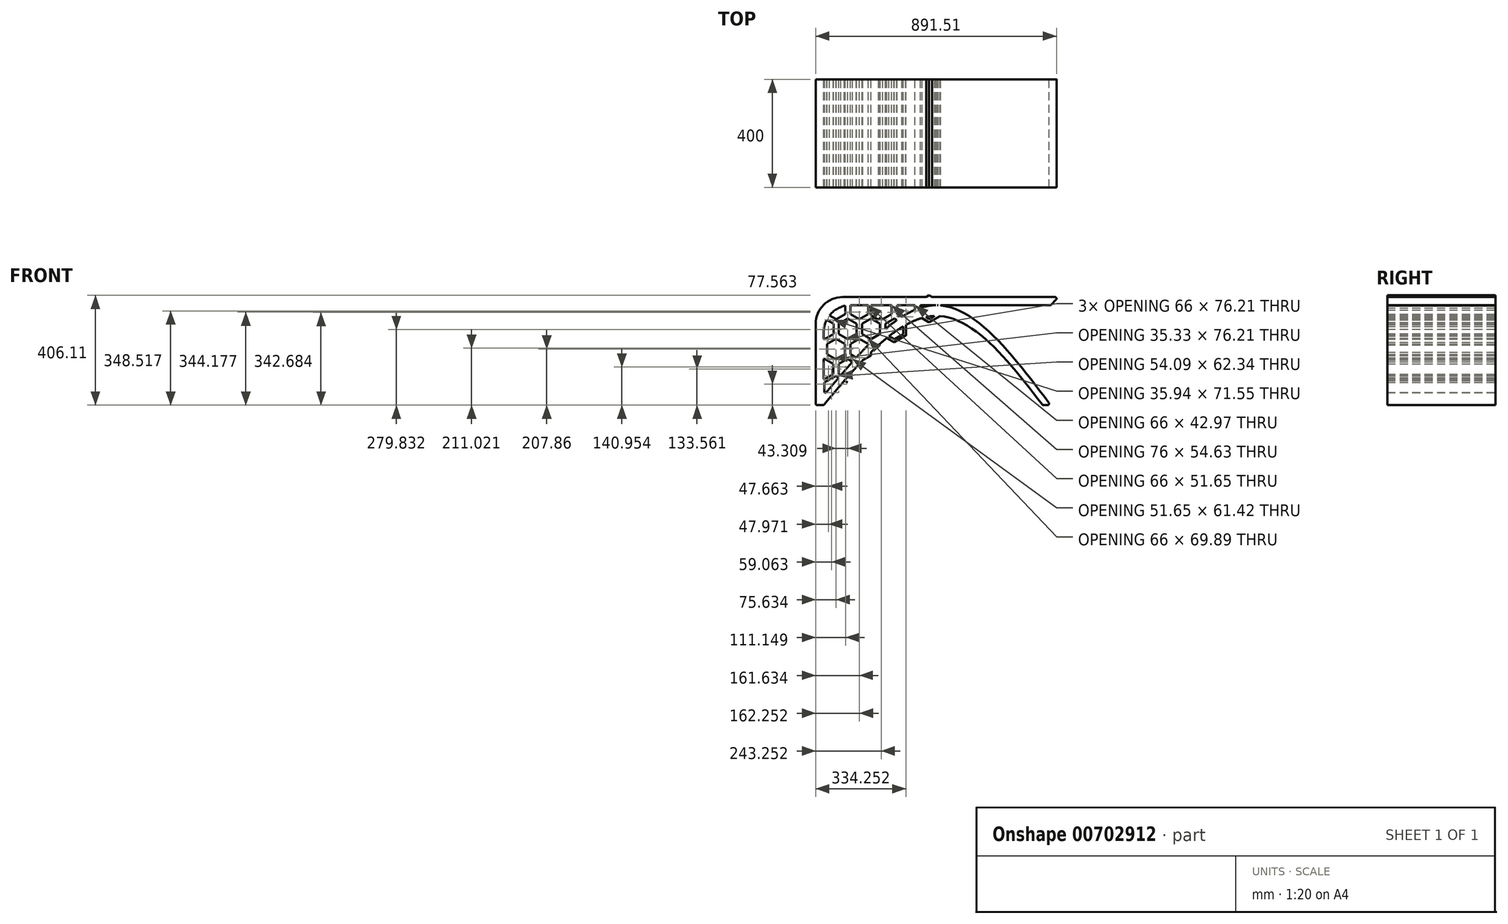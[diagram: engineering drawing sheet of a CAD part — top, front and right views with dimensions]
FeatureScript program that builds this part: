
annotation { "Feature Type Name" : "Feature", "Feature Type Description" : "" }
export const myFeature = defineFeature(function(context is Context, id is Id, definition is map)
    precondition{}
    {
        {
            var Q0;
            Q0=qCreatedBy(makeId("Front.planeOp"),FACE);
            var sketch = newSketch(context, id + "F0", { "sketchPlane" : qUnion([Q0])});
            skLineSegment(sketch, "E0", {"start": v(450, 0) * mm, "end": v(-450, 0) * mm});
            skLineSegment(sketch, "E1", {"start": v(-450, 0) * mm, "end": v(-450, -400) * mm});
            skLineSegment(sketch, "E2.0", {"start": v(-420, -30) * mm, "end": v(-420, -364.15) * mm});
            skLineSegment(sketch, "E2.1", {"start": v(420, -30) * mm, "end": v(-420, -30) * mm});
            skPoint(sketch, "E3.1.internal.snap0", {"position": v(0, -30) * mm});
            skLineSegment(sketch, "E4", {"start": v(-450, -400) * mm, "end": v(-420, -400) * mm});
            skLineSegment(sketch, "E5", {"start": v(390, -400) * mm, "end": v(420, -400) * mm});
            skLineSegment(sketch, "E6", {"start": v(450, 0) * mm, "end": v(420, -30) * mm});
            skFitSpline(sketch, "E7", {"points": [v(-420, -400) * mm, v(0, -70) * mm, v(390, -400) * mm], "startDerivative": vector(822.55, 1000.92) * mm, "endDerivative": vector(763.86, -1006.69) * mm});
            skFitSpline(sketch, "E8", {"points": [v(-450, -400) * mm, v(0, -30) * mm, v(420, -400) * mm], "startDerivative": vector(902.18, 1075.28) * mm, "endDerivative": vector(817.43, -1085.12) * mm});
            skSolve(sketch);
        }
        {
            var Q0;
            Q0 = qSketchRegion(id + "F0", true);
            extrude(context, id + "F1", {"entities" : qUnion([Q0]), "depth" : 400 * mm, "offsetDistance" : 25 * mm});
        }
        {
            var Q0;
            Q0=makeQuery(id+"F1.opExtrude","SWEPT_EDGE",EDGE,{"disambiguationData":[OSD([sQuery(id+"F0.wireOp",EDGE,"E0"),sQuery(id+"F0.wireOp",EDGE,"E1")])]});
            var Q1;
            Q1=makeQuery(id+"F1.opExtrude","SWEPT_EDGE",EDGE,{"disambiguationData":[OSD([sQuery(id+"F0.wireOp",EDGE,"E2.0"),sQuery(id+"F0.wireOp",EDGE,"E2.1")])]});
            fillet(context, id + "F2", {"entities" : qUnion([Q0, Q1]), "radius" : 100 * mm, "tangentPropagation" : true, "allowEdgeOverflow" : false});
        }
        {
            var Q0;
            Q0=makeQuery(id+"F1.opExtrude","SWEPT_EDGE",EDGE,{"disambiguationData":[OSD([sQuery(id+"F0.wireOp",EDGE,"E1"),sQuery(id+"F0.wireOp",EDGE,"E4")])]});
            var Q1;
            Q1=makeQuery(id+"F1.opExtrude","SWEPT_EDGE",EDGE,{"disambiguationData":[OSD([sQuery(id+"F0.wireOp",EDGE,"E4"),sQuery(id+"F0.wireOp",EDGE,"E7")])]});
            var Q2;
            Q2=makeQuery(id+"F1.opExtrude","SWEPT_EDGE",EDGE,{"disambiguationData":[OSD([sQuery(id+"F0.wireOp",EDGE,"E5"),sQuery(id+"F0.wireOp",EDGE,"E7")])]});
            var Q3;
            Q3=makeQuery(id+"F1.opExtrude","SWEPT_EDGE",EDGE,{"disambiguationData":[OSD([sQuery(id+"F0.wireOp",EDGE,"E5"),sQuery(id+"F0.wireOp",EDGE,"eab066b6-30cd-4fa4-bec9-29529f9bb2eb")])]});
            var Q4;
            Q4=makeQuery(id+"F1.opExtrude","SWEPT_EDGE",EDGE,{"disambiguationData":[OSD([sQuery(id+"F0.wireOp",EDGE,"E0"),sQuery(id+"F0.wireOp",EDGE,"E6")])]});
            var Q5;
            Q5=makeQuery(id+"F1.opExtrude","SWEPT_EDGE",EDGE,{"disambiguationData":[OSD([sQuery(id+"F0.wireOp",EDGE,"E2.1"),sQuery(id+"F0.wireOp",EDGE,"E6")])]});
            var Q6;
            Q6=makeQuery(id+"F1.opExtrude","SWEPT_EDGE",EDGE,{"disambiguationData":[OSD([sQuery(id+"F0.wireOp",EDGE,"E2.0"),sQuery(id+"F0.wireOp",EDGE,"E8")])]});
            fillet(context, id + "F3", {"entities" : qUnion([Q0, Q1, Q2, Q3, Q4, Q5, Q6]), "radius" : 6 * mm, "tangentPropagation" : true, "allowEdgeOverflow" : false});
        }
        {
            var Q0;
            Q0=qCreatedBy(makeId("Front.planeOp"),FACE);
            var sketch = newSketch(context, id + "F4", { "sketchPlane" : qUnion([Q0])});
            skCircle(sketch, "E9.cCircle", {"center": v(-29.75, -43.54) * mm, "radius": 33 * mm, "construction": true});
            skLineSegment(sketch, "E9.0", {"start": v(3.25, -62.6) * mm, "end": v(-29.75, -81.65) * mm});
            skLineSegment(sketch, "E9.1", {"start": v(-29.75, -81.65) * mm, "end": v(-62.75, -62.6) * mm});
            skLineSegment(sketch, "E9.2", {"start": v(-62.75, -62.6) * mm, "end": v(-62.75, -24.49) * mm});
            skLineSegment(sketch, "E9.3", {"start": v(-62.75, -24.49) * mm, "end": v(-29.75, -5.44) * mm});
            skLineSegment(sketch, "E9.4", {"start": v(-29.75, -5.44) * mm, "end": v(3.25, -24.49) * mm});
            skLineSegment(sketch, "E9.5", {"start": v(3.25, -24.49) * mm, "end": v(3.25, -62.6) * mm});
            skPoint(sketch, "E9.0.midPoint", {"position": v(-13.25, -72.12) * mm});
            skLineSegment(sketch, "E10.0", {"start": v(-72.75, -68.37) * mm, "end": v(-72.75, -18.72) * mm});
            skLineSegment(sketch, "E10.1", {"start": v(-29.75, 6.11) * mm, "end": v(13.25, -18.72) * mm});
            skLineSegment(sketch, "E10.2", {"start": v(13.25, -18.72) * mm, "end": v(13.25, -68.37) * mm});
            skLineSegment(sketch, "E10.3", {"start": v(-72.75, -18.72) * mm, "end": v(-29.75, 6.11) * mm});
            skLineSegment(sketch, "E10.4", {"start": v(13.25, -68.37) * mm, "end": v(-29.75, -93.2) * mm});
            skLineSegment(sketch, "E10.5", {"start": v(-29.75, -93.2) * mm, "end": v(-72.75, -68.37) * mm});
            skLineSegment(sketch, "E11.0.1.0", {"start": v(-73.06, -167.5) * mm, "end": v(-116.06, -142.67) * mm});
            skLineSegment(sketch, "E11.0.1.1", {"start": v(-30.06, -142.67) * mm, "end": v(-73.06, -167.5) * mm});
            skLineSegment(sketch, "E11.0.1.2", {"start": v(-116.06, -93.01) * mm, "end": v(-73.06, -68.19) * mm});
            skLineSegment(sketch, "E11.0.1.3", {"start": v(-30.06, -93.01) * mm, "end": v(-30.06, -142.67) * mm});
            skLineSegment(sketch, "E11.0.1.4", {"start": v(-73.06, -68.19) * mm, "end": v(-30.06, -93.01) * mm});
            skLineSegment(sketch, "E11.0.1.5", {"start": v(-116.06, -142.67) * mm, "end": v(-116.06, -93.01) * mm});
            skLineSegment(sketch, "E11.0.1.6", {"start": v(-40.06, -98.79) * mm, "end": v(-40.06, -136.9) * mm});
            skLineSegment(sketch, "E11.0.1.7", {"start": v(-73.06, -79.74) * mm, "end": v(-40.06, -98.79) * mm});
            skLineSegment(sketch, "E11.0.1.8", {"start": v(-106.06, -98.79) * mm, "end": v(-73.06, -79.74) * mm});
            skLineSegment(sketch, "E11.0.1.9", {"start": v(-106.06, -136.9) * mm, "end": v(-106.06, -98.79) * mm});
            skLineSegment(sketch, "E11.0.1.10", {"start": v(-73.06, -155.95) * mm, "end": v(-106.06, -136.9) * mm});
            skLineSegment(sketch, "E11.0.1.11", {"start": v(-40.06, -136.9) * mm, "end": v(-73.06, -155.95) * mm});
            skCircle(sketch, "E11.0.1.12", {"center": v(-73.06, -117.84) * mm, "radius": 33 * mm, "construction": true});
            skPoint(sketch, "E11.0.1.13", {"position": v(-56.56, -146.42) * mm});
            skLineSegment(sketch, "E11.0.2.0", {"start": v(-116.37, -241.8) * mm, "end": v(-159.37, -216.97) * mm});
            skLineSegment(sketch, "E11.0.2.1", {"start": v(-73.37, -216.97) * mm, "end": v(-116.37, -241.8) * mm});
            skLineSegment(sketch, "E11.0.2.2", {"start": v(-159.37, -167.31) * mm, "end": v(-116.37, -142.49) * mm});
            skLineSegment(sketch, "E11.0.2.3", {"start": v(-73.37, -167.31) * mm, "end": v(-73.37, -216.97) * mm});
            skLineSegment(sketch, "E11.0.2.4", {"start": v(-116.37, -142.49) * mm, "end": v(-73.37, -167.31) * mm});
            skLineSegment(sketch, "E11.0.2.5", {"start": v(-159.37, -216.97) * mm, "end": v(-159.37, -167.31) * mm});
            skLineSegment(sketch, "E11.0.2.6", {"start": v(-83.37, -173.09) * mm, "end": v(-83.37, -211.2) * mm});
            skLineSegment(sketch, "E11.0.2.7", {"start": v(-116.37, -154.03) * mm, "end": v(-83.37, -173.09) * mm});
            skLineSegment(sketch, "E11.0.2.8", {"start": v(-149.37, -173.09) * mm, "end": v(-116.37, -154.03) * mm});
            skLineSegment(sketch, "E11.0.2.9", {"start": v(-149.37, -211.2) * mm, "end": v(-149.37, -173.09) * mm});
            skLineSegment(sketch, "E11.0.2.10", {"start": v(-116.37, -230.24) * mm, "end": v(-149.37, -211.2) * mm});
            skLineSegment(sketch, "E11.0.2.11", {"start": v(-83.37, -211.2) * mm, "end": v(-116.37, -230.24) * mm});
            skCircle(sketch, "E11.0.2.12", {"center": v(-116.37, -192.14) * mm, "radius": 33 * mm, "construction": true});
            skPoint(sketch, "E11.0.2.13", {"position": v(-99.87, -220.72) * mm});
            skLineSegment(sketch, "E11.0.3.2", {"start": v(-202.67, -241.61) * mm, "end": v(-159.67, -216.79) * mm});
            skLineSegment(sketch, "E11.0.3.3", {"start": v(-116.67, -241.61) * mm, "end": v(-116.67, -291.26) * mm});
            skLineSegment(sketch, "E11.0.3.4", {"start": v(-159.67, -216.79) * mm, "end": v(-116.67, -241.61) * mm});
            skLineSegment(sketch, "E11.0.3.5", {"start": v(-202.67, -291.26) * mm, "end": v(-202.67, -241.61) * mm});
            skLineSegment(sketch, "E11.0.3.6", {"start": v(-126.67, -247.39) * mm, "end": v(-126.67, -285.5) * mm});
            skLineSegment(sketch, "E11.0.3.7", {"start": v(-159.67, -228.33) * mm, "end": v(-126.67, -247.39) * mm});
            skLineSegment(sketch, "E11.0.3.8", {"start": v(-192.67, -247.39) * mm, "end": v(-159.67, -228.33) * mm});
            skLineSegment(sketch, "E11.0.3.9", {"start": v(-192.67, -285.5) * mm, "end": v(-192.67, -247.39) * mm});
            skCircle(sketch, "E11.0.3.12", {"center": v(-159.67, -266.44) * mm, "radius": 33 * mm, "construction": true});
            skLineSegment(sketch, "E11.1.0.0", {"start": v(-115.75, -93.2) * mm, "end": v(-158.75, -68.37) * mm});
            skLineSegment(sketch, "E11.1.0.1", {"start": v(-72.75, -68.37) * mm, "end": v(-115.75, -93.2) * mm});
            skLineSegment(sketch, "E11.1.0.2", {"start": v(-158.75, -18.72) * mm, "end": v(-115.75, 6.11) * mm});
            skLineSegment(sketch, "E11.1.0.3", {"start": v(-72.75, -18.72) * mm, "end": v(-72.75, -68.37) * mm});
            skLineSegment(sketch, "E11.1.0.4", {"start": v(-115.75, 6.11) * mm, "end": v(-72.75, -18.72) * mm});
            skLineSegment(sketch, "E11.1.0.5", {"start": v(-158.75, -68.37) * mm, "end": v(-158.75, -18.72) * mm});
            skLineSegment(sketch, "E11.1.0.6", {"start": v(-82.75, -24.49) * mm, "end": v(-82.75, -62.6) * mm});
            skLineSegment(sketch, "E11.1.0.7", {"start": v(-115.75, -5.44) * mm, "end": v(-82.75, -24.49) * mm});
            skLineSegment(sketch, "E11.1.0.8", {"start": v(-148.75, -24.49) * mm, "end": v(-115.75, -5.44) * mm});
            skLineSegment(sketch, "E11.1.0.9", {"start": v(-148.75, -62.6) * mm, "end": v(-148.75, -24.49) * mm});
            skLineSegment(sketch, "E11.1.0.10", {"start": v(-115.75, -81.65) * mm, "end": v(-148.75, -62.6) * mm});
            skLineSegment(sketch, "E11.1.0.11", {"start": v(-82.75, -62.6) * mm, "end": v(-115.75, -81.65) * mm});
            skCircle(sketch, "E11.1.0.12", {"center": v(-115.75, -43.54) * mm, "radius": 33 * mm, "construction": true});
            skPoint(sketch, "E11.1.0.13", {"position": v(-99.25, -72.12) * mm});
            skLineSegment(sketch, "E11.1.1.0", {"start": v(-159.06, -167.5) * mm, "end": v(-202.06, -142.67) * mm});
            skLineSegment(sketch, "E11.1.1.1", {"start": v(-116.06, -142.67) * mm, "end": v(-159.06, -167.5) * mm});
            skLineSegment(sketch, "E11.1.1.2", {"start": v(-202.06, -93.01) * mm, "end": v(-159.06, -68.19) * mm});
            skLineSegment(sketch, "E11.1.1.3", {"start": v(-116.06, -93.01) * mm, "end": v(-116.06, -142.67) * mm});
            skLineSegment(sketch, "E11.1.1.4", {"start": v(-159.06, -68.19) * mm, "end": v(-116.06, -93.01) * mm});
            skLineSegment(sketch, "E11.1.1.5", {"start": v(-202.06, -142.67) * mm, "end": v(-202.06, -93.01) * mm});
            skLineSegment(sketch, "E11.1.1.6", {"start": v(-126.06, -98.79) * mm, "end": v(-126.06, -136.9) * mm});
            skLineSegment(sketch, "E11.1.1.7", {"start": v(-159.06, -79.74) * mm, "end": v(-126.06, -98.79) * mm});
            skLineSegment(sketch, "E11.1.1.8", {"start": v(-192.06, -98.79) * mm, "end": v(-159.06, -79.74) * mm});
            skLineSegment(sketch, "E11.1.1.9", {"start": v(-192.06, -136.9) * mm, "end": v(-192.06, -98.79) * mm});
            skLineSegment(sketch, "E11.1.1.10", {"start": v(-159.06, -155.95) * mm, "end": v(-192.06, -136.9) * mm});
            skLineSegment(sketch, "E11.1.1.11", {"start": v(-126.06, -136.9) * mm, "end": v(-159.06, -155.95) * mm});
            skCircle(sketch, "E11.1.1.12", {"center": v(-159.06, -117.84) * mm, "radius": 33 * mm, "construction": true});
            skPoint(sketch, "E11.1.1.13", {"position": v(-142.56, -146.42) * mm});
            skLineSegment(sketch, "E11.1.2.0", {"start": v(-202.37, -241.8) * mm, "end": v(-245.37, -216.97) * mm});
            skLineSegment(sketch, "E11.1.2.1", {"start": v(-159.37, -216.97) * mm, "end": v(-202.37, -241.8) * mm});
            skLineSegment(sketch, "E11.1.2.2", {"start": v(-245.37, -167.31) * mm, "end": v(-202.37, -142.49) * mm});
            skLineSegment(sketch, "E11.1.2.3", {"start": v(-159.37, -167.31) * mm, "end": v(-159.37, -216.97) * mm});
            skLineSegment(sketch, "E11.1.2.4", {"start": v(-202.37, -142.49) * mm, "end": v(-159.37, -167.31) * mm});
            skLineSegment(sketch, "E11.1.2.5", {"start": v(-245.37, -216.97) * mm, "end": v(-245.37, -167.31) * mm});
            skLineSegment(sketch, "E11.1.2.6", {"start": v(-169.37, -173.09) * mm, "end": v(-169.37, -211.2) * mm});
            skLineSegment(sketch, "E11.1.2.7", {"start": v(-202.37, -154.03) * mm, "end": v(-169.37, -173.09) * mm});
            skLineSegment(sketch, "E11.1.2.8", {"start": v(-235.37, -173.09) * mm, "end": v(-202.37, -154.03) * mm});
            skLineSegment(sketch, "E11.1.2.9", {"start": v(-235.37, -211.2) * mm, "end": v(-235.37, -173.09) * mm});
            skLineSegment(sketch, "E11.1.2.10", {"start": v(-202.37, -230.24) * mm, "end": v(-235.37, -211.2) * mm});
            skLineSegment(sketch, "E11.1.2.11", {"start": v(-169.37, -211.2) * mm, "end": v(-202.37, -230.24) * mm});
            skCircle(sketch, "E11.1.2.12", {"center": v(-202.37, -192.14) * mm, "radius": 33 * mm, "construction": true});
            skPoint(sketch, "E11.1.2.13", {"position": v(-185.87, -220.72) * mm});
            skLineSegment(sketch, "E11.1.3.2", {"start": v(-288.67, -241.61) * mm, "end": v(-245.67, -216.79) * mm});
            skLineSegment(sketch, "E11.1.3.3", {"start": v(-202.67, -241.61) * mm, "end": v(-202.67, -291.26) * mm});
            skLineSegment(sketch, "E11.1.3.4", {"start": v(-245.67, -216.79) * mm, "end": v(-202.67, -241.61) * mm});
            skLineSegment(sketch, "E11.1.3.5", {"start": v(-288.67, -291.26) * mm, "end": v(-288.67, -241.61) * mm});
            skLineSegment(sketch, "E11.1.3.6", {"start": v(-212.67, -247.39) * mm, "end": v(-212.67, -285.5) * mm});
            skLineSegment(sketch, "E11.1.3.7", {"start": v(-245.67, -228.33) * mm, "end": v(-212.67, -247.39) * mm});
            skLineSegment(sketch, "E11.1.3.8", {"start": v(-278.67, -247.39) * mm, "end": v(-245.67, -228.33) * mm});
            skLineSegment(sketch, "E11.1.3.9", {"start": v(-278.67, -285.5) * mm, "end": v(-278.67, -247.39) * mm});
            skCircle(sketch, "E11.1.3.12", {"center": v(-245.67, -266.44) * mm, "radius": 33 * mm, "construction": true});
            skLineSegment(sketch, "E11.1.4.2", {"start": v(-331.98, -315.91) * mm, "end": v(-288.98, -291.09) * mm});
            skLineSegment(sketch, "E11.1.4.5", {"start": v(-331.98, -315.91) * mm, "end": v(-331.98, -315.91) * mm});
            skLineSegment(sketch, "E11.1.4.8", {"start": v(-321.98, -321.69) * mm, "end": v(-288.98, -302.63) * mm});
            skLineSegment(sketch, "E11.1.4.9", {"start": v(-321.98, -359.8) * mm, "end": v(-321.98, -321.69) * mm});
            skLineSegment(sketch, "E11.1.4.10", {"start": v(-288.98, -378.84) * mm, "end": v(-321.98, -359.8) * mm});
            skCircle(sketch, "E11.1.4.12", {"center": v(-288.98, -340.74) * mm, "radius": 33 * mm, "construction": true});
            skLineSegment(sketch, "E11.2.0.0", {"start": v(-201.75, -93.2) * mm, "end": v(-244.75, -68.37) * mm});
            skLineSegment(sketch, "E11.2.0.1", {"start": v(-158.75, -68.37) * mm, "end": v(-201.75, -93.2) * mm});
            skLineSegment(sketch, "E11.2.0.2", {"start": v(-244.75, -18.72) * mm, "end": v(-201.75, 6.11) * mm});
            skLineSegment(sketch, "E11.2.0.3", {"start": v(-158.75, -18.72) * mm, "end": v(-158.75, -68.37) * mm});
            skLineSegment(sketch, "E11.2.0.4", {"start": v(-201.75, 6.11) * mm, "end": v(-158.75, -18.72) * mm});
            skLineSegment(sketch, "E11.2.0.5", {"start": v(-244.75, -68.37) * mm, "end": v(-244.75, -18.72) * mm});
            skLineSegment(sketch, "E11.2.0.6", {"start": v(-168.75, -24.49) * mm, "end": v(-168.75, -62.6) * mm});
            skLineSegment(sketch, "E11.2.0.7", {"start": v(-201.75, -5.44) * mm, "end": v(-168.75, -24.49) * mm});
            skLineSegment(sketch, "E11.2.0.8", {"start": v(-234.75, -24.49) * mm, "end": v(-201.75, -5.44) * mm});
            skLineSegment(sketch, "E11.2.0.9", {"start": v(-234.75, -62.6) * mm, "end": v(-234.75, -24.49) * mm});
            skLineSegment(sketch, "E11.2.0.10", {"start": v(-201.75, -81.65) * mm, "end": v(-234.75, -62.6) * mm});
            skLineSegment(sketch, "E11.2.0.11", {"start": v(-168.75, -62.6) * mm, "end": v(-201.75, -81.65) * mm});
            skCircle(sketch, "E11.2.0.12", {"center": v(-201.75, -43.54) * mm, "radius": 33 * mm, "construction": true});
            skPoint(sketch, "E11.2.0.13", {"position": v(-185.25, -72.12) * mm});
            skLineSegment(sketch, "E11.2.1.0", {"start": v(-245.06, -167.5) * mm, "end": v(-288.06, -142.67) * mm});
            skLineSegment(sketch, "E11.2.1.1", {"start": v(-202.06, -142.67) * mm, "end": v(-245.06, -167.5) * mm});
            skLineSegment(sketch, "E11.2.1.2", {"start": v(-288.06, -93.01) * mm, "end": v(-245.06, -68.19) * mm});
            skLineSegment(sketch, "E11.2.1.3", {"start": v(-202.06, -93.01) * mm, "end": v(-202.06, -142.67) * mm});
            skLineSegment(sketch, "E11.2.1.4", {"start": v(-245.06, -68.19) * mm, "end": v(-202.06, -93.01) * mm});
            skLineSegment(sketch, "E11.2.1.5", {"start": v(-288.06, -142.67) * mm, "end": v(-288.06, -93.01) * mm});
            skLineSegment(sketch, "E11.2.1.6", {"start": v(-212.06, -98.79) * mm, "end": v(-212.06, -136.9) * mm});
            skLineSegment(sketch, "E11.2.1.7", {"start": v(-245.06, -79.74) * mm, "end": v(-212.06, -98.79) * mm});
            skLineSegment(sketch, "E11.2.1.8", {"start": v(-278.06, -98.79) * mm, "end": v(-245.06, -79.74) * mm});
            skLineSegment(sketch, "E11.2.1.9", {"start": v(-278.06, -136.9) * mm, "end": v(-278.06, -98.79) * mm});
            skLineSegment(sketch, "E11.2.1.10", {"start": v(-245.06, -155.95) * mm, "end": v(-278.06, -136.9) * mm});
            skLineSegment(sketch, "E11.2.1.11", {"start": v(-212.06, -136.9) * mm, "end": v(-245.06, -155.95) * mm});
            skCircle(sketch, "E11.2.1.12", {"center": v(-245.06, -117.84) * mm, "radius": 33 * mm, "construction": true});
            skPoint(sketch, "E11.2.1.13", {"position": v(-228.56, -146.42) * mm});
            skLineSegment(sketch, "E11.2.2.0", {"start": v(-288.37, -241.8) * mm, "end": v(-331.37, -216.97) * mm});
            skLineSegment(sketch, "E11.2.2.1", {"start": v(-245.37, -216.97) * mm, "end": v(-288.37, -241.8) * mm});
            skLineSegment(sketch, "E11.2.2.2", {"start": v(-331.37, -167.31) * mm, "end": v(-288.37, -142.49) * mm});
            skLineSegment(sketch, "E11.2.2.3", {"start": v(-245.37, -167.31) * mm, "end": v(-245.37, -216.97) * mm});
            skLineSegment(sketch, "E11.2.2.4", {"start": v(-288.37, -142.49) * mm, "end": v(-245.37, -167.31) * mm});
            skLineSegment(sketch, "E11.2.2.5", {"start": v(-331.37, -216.97) * mm, "end": v(-331.37, -167.31) * mm});
            skLineSegment(sketch, "E11.2.2.6", {"start": v(-255.37, -173.09) * mm, "end": v(-255.37, -211.2) * mm});
            skLineSegment(sketch, "E11.2.2.7", {"start": v(-288.37, -154.03) * mm, "end": v(-255.37, -173.09) * mm});
            skLineSegment(sketch, "E11.2.2.8", {"start": v(-321.37, -173.09) * mm, "end": v(-288.37, -154.03) * mm});
            skLineSegment(sketch, "E11.2.2.9", {"start": v(-321.37, -211.2) * mm, "end": v(-321.37, -173.09) * mm});
            skLineSegment(sketch, "E11.2.2.10", {"start": v(-288.37, -230.24) * mm, "end": v(-321.37, -211.2) * mm});
            skLineSegment(sketch, "E11.2.2.11", {"start": v(-255.37, -211.2) * mm, "end": v(-288.37, -230.24) * mm});
            skCircle(sketch, "E11.2.2.12", {"center": v(-288.37, -192.14) * mm, "radius": 33 * mm, "construction": true});
            skPoint(sketch, "E11.2.2.13", {"position": v(-271.87, -220.72) * mm});
            skLineSegment(sketch, "E11.2.3.0", {"start": v(-331.67, -316.1) * mm, "end": v(-374.67, -291.26) * mm});
            skLineSegment(sketch, "E11.2.3.1", {"start": v(-288.67, -291.26) * mm, "end": v(-331.67, -316.1) * mm});
            skLineSegment(sketch, "E11.2.3.2", {"start": v(-374.67, -241.61) * mm, "end": v(-331.67, -216.79) * mm});
            skLineSegment(sketch, "E11.2.3.3", {"start": v(-288.67, -241.61) * mm, "end": v(-288.67, -291.26) * mm});
            skLineSegment(sketch, "E11.2.3.4", {"start": v(-331.67, -216.79) * mm, "end": v(-288.67, -241.61) * mm});
            skLineSegment(sketch, "E11.2.3.5", {"start": v(-374.67, -291.26) * mm, "end": v(-374.67, -241.61) * mm});
            skLineSegment(sketch, "E11.2.3.6", {"start": v(-298.67, -247.39) * mm, "end": v(-298.67, -285.5) * mm});
            skLineSegment(sketch, "E11.2.3.7", {"start": v(-331.67, -228.33) * mm, "end": v(-298.67, -247.39) * mm});
            skLineSegment(sketch, "E11.2.3.8", {"start": v(-364.67, -247.39) * mm, "end": v(-331.67, -228.33) * mm});
            skLineSegment(sketch, "E11.2.3.9", {"start": v(-364.67, -285.5) * mm, "end": v(-364.67, -247.39) * mm});
            skLineSegment(sketch, "E11.2.3.10", {"start": v(-331.67, -304.54) * mm, "end": v(-364.67, -285.5) * mm});
            skLineSegment(sketch, "E11.2.3.11", {"start": v(-298.67, -285.5) * mm, "end": v(-331.67, -304.54) * mm});
            skCircle(sketch, "E11.2.3.12", {"center": v(-331.67, -266.44) * mm, "radius": 33 * mm, "construction": true});
            skPoint(sketch, "E11.2.3.13", {"position": v(-315.17, -295.02) * mm});
            skLineSegment(sketch, "E11.2.4.2", {"start": v(-417.98, -315.91) * mm, "end": v(-374.98, -291.09) * mm});
            skLineSegment(sketch, "E11.2.4.3", {"start": v(-331.98, -315.91) * mm, "end": v(-331.98, -365.56) * mm});
            skLineSegment(sketch, "E11.2.4.4", {"start": v(-374.98, -291.09) * mm, "end": v(-331.98, -315.91) * mm});
            skLineSegment(sketch, "E11.2.4.5", {"start": v(-417.98, -365.56) * mm, "end": v(-417.98, -315.91) * mm});
            skLineSegment(sketch, "E11.2.4.6", {"start": v(-341.98, -321.69) * mm, "end": v(-341.98, -359.8) * mm});
            skLineSegment(sketch, "E11.2.4.7", {"start": v(-374.98, -302.63) * mm, "end": v(-341.98, -321.69) * mm});
            skLineSegment(sketch, "E11.2.4.8", {"start": v(-407.98, -321.69) * mm, "end": v(-374.98, -302.63) * mm});
            skLineSegment(sketch, "E11.2.4.9", {"start": v(-407.98, -359.8) * mm, "end": v(-407.98, -321.69) * mm});
            skLineSegment(sketch, "E11.2.4.10", {"start": v(-374.98, -378.84) * mm, "end": v(-407.98, -359.8) * mm});
            skLineSegment(sketch, "E11.2.4.11", {"start": v(-341.98, -359.8) * mm, "end": v(-374.98, -378.84) * mm});
            skCircle(sketch, "E11.2.4.12", {"center": v(-374.98, -340.74) * mm, "radius": 33 * mm, "construction": true});
            skPoint(sketch, "E11.2.4.13", {"position": v(-358.48, -369.32) * mm});
            skLineSegment(sketch, "E11.3.0.0", {"start": v(-287.75, -93.2) * mm, "end": v(-330.75, -68.37) * mm});
            skLineSegment(sketch, "E11.3.0.1", {"start": v(-244.75, -68.37) * mm, "end": v(-287.75, -93.2) * mm});
            skLineSegment(sketch, "E11.3.0.2", {"start": v(-330.75, -18.72) * mm, "end": v(-287.75, 6.11) * mm});
            skLineSegment(sketch, "E11.3.0.3", {"start": v(-244.75, -18.72) * mm, "end": v(-244.75, -68.37) * mm});
            skLineSegment(sketch, "E11.3.0.4", {"start": v(-287.75, 6.11) * mm, "end": v(-244.75, -18.72) * mm});
            skLineSegment(sketch, "E11.3.0.5", {"start": v(-330.75, -68.37) * mm, "end": v(-330.75, -18.72) * mm});
            skLineSegment(sketch, "E11.3.0.6", {"start": v(-254.75, -24.49) * mm, "end": v(-254.75, -62.6) * mm});
            skLineSegment(sketch, "E11.3.0.7", {"start": v(-287.75, -5.44) * mm, "end": v(-254.75, -24.49) * mm});
            skLineSegment(sketch, "E11.3.0.8", {"start": v(-320.75, -24.49) * mm, "end": v(-287.75, -5.44) * mm});
            skLineSegment(sketch, "E11.3.0.9", {"start": v(-320.75, -62.6) * mm, "end": v(-320.75, -24.49) * mm});
            skLineSegment(sketch, "E11.3.0.10", {"start": v(-287.75, -81.65) * mm, "end": v(-320.75, -62.6) * mm});
            skLineSegment(sketch, "E11.3.0.11", {"start": v(-254.75, -62.6) * mm, "end": v(-287.75, -81.65) * mm});
            skCircle(sketch, "E11.3.0.12", {"center": v(-287.75, -43.54) * mm, "radius": 33 * mm, "construction": true});
            skPoint(sketch, "E11.3.0.13", {"position": v(-271.25, -72.12) * mm});
            skLineSegment(sketch, "E11.3.1.0", {"start": v(-331.06, -167.5) * mm, "end": v(-374.06, -142.67) * mm});
            skLineSegment(sketch, "E11.3.1.1", {"start": v(-288.06, -142.67) * mm, "end": v(-331.06, -167.5) * mm});
            skLineSegment(sketch, "E11.3.1.2", {"start": v(-374.06, -93.01) * mm, "end": v(-331.06, -68.19) * mm});
            skLineSegment(sketch, "E11.3.1.3", {"start": v(-288.06, -93.01) * mm, "end": v(-288.06, -142.67) * mm});
            skLineSegment(sketch, "E11.3.1.4", {"start": v(-331.06, -68.19) * mm, "end": v(-288.06, -93.01) * mm});
            skLineSegment(sketch, "E11.3.1.5", {"start": v(-374.06, -142.67) * mm, "end": v(-374.06, -93.01) * mm});
            skLineSegment(sketch, "E11.3.1.6", {"start": v(-298.06, -98.79) * mm, "end": v(-298.06, -136.9) * mm});
            skLineSegment(sketch, "E11.3.1.7", {"start": v(-331.06, -79.74) * mm, "end": v(-298.06, -98.79) * mm});
            skLineSegment(sketch, "E11.3.1.8", {"start": v(-364.06, -98.79) * mm, "end": v(-331.06, -79.74) * mm});
            skLineSegment(sketch, "E11.3.1.9", {"start": v(-364.06, -136.9) * mm, "end": v(-364.06, -98.79) * mm});
            skLineSegment(sketch, "E11.3.1.10", {"start": v(-331.06, -155.95) * mm, "end": v(-364.06, -136.9) * mm});
            skLineSegment(sketch, "E11.3.1.11", {"start": v(-298.06, -136.9) * mm, "end": v(-331.06, -155.95) * mm});
            skCircle(sketch, "E11.3.1.12", {"center": v(-331.06, -117.84) * mm, "radius": 33 * mm, "construction": true});
            skPoint(sketch, "E11.3.1.13", {"position": v(-314.56, -146.42) * mm});
            skLineSegment(sketch, "E11.3.2.0", {"start": v(-374.37, -241.8) * mm, "end": v(-417.37, -216.97) * mm});
            skLineSegment(sketch, "E11.3.2.1", {"start": v(-331.37, -216.97) * mm, "end": v(-374.37, -241.8) * mm});
            skLineSegment(sketch, "E11.3.2.2", {"start": v(-417.37, -167.31) * mm, "end": v(-374.37, -142.49) * mm});
            skLineSegment(sketch, "E11.3.2.3", {"start": v(-331.37, -167.31) * mm, "end": v(-331.37, -216.97) * mm});
            skLineSegment(sketch, "E11.3.2.4", {"start": v(-374.37, -142.49) * mm, "end": v(-331.37, -167.31) * mm});
            skLineSegment(sketch, "E11.3.2.5", {"start": v(-417.37, -216.97) * mm, "end": v(-417.37, -167.31) * mm});
            skLineSegment(sketch, "E11.3.2.6", {"start": v(-341.37, -173.09) * mm, "end": v(-341.37, -211.2) * mm});
            skLineSegment(sketch, "E11.3.2.7", {"start": v(-374.37, -154.03) * mm, "end": v(-341.37, -173.09) * mm});
            skLineSegment(sketch, "E11.3.2.8", {"start": v(-407.37, -173.09) * mm, "end": v(-374.37, -154.03) * mm});
            skLineSegment(sketch, "E11.3.2.9", {"start": v(-407.37, -211.2) * mm, "end": v(-407.37, -173.09) * mm});
            skLineSegment(sketch, "E11.3.2.10", {"start": v(-374.37, -230.24) * mm, "end": v(-407.37, -211.2) * mm});
            skLineSegment(sketch, "E11.3.2.11", {"start": v(-341.37, -211.2) * mm, "end": v(-374.37, -230.24) * mm});
            skCircle(sketch, "E11.3.2.12", {"center": v(-374.37, -192.14) * mm, "radius": 33 * mm, "construction": true});
            skPoint(sketch, "E11.3.2.13", {"position": v(-357.87, -220.72) * mm});
            skLineSegment(sketch, "E11.3.3.0", {"start": v(-417.67, -316.1) * mm, "end": v(-460.67, -291.26) * mm});
            skLineSegment(sketch, "E11.3.3.1", {"start": v(-374.67, -291.26) * mm, "end": v(-417.67, -316.1) * mm});
            skLineSegment(sketch, "E11.3.3.2", {"start": v(-460.67, -241.61) * mm, "end": v(-417.67, -216.79) * mm});
            skLineSegment(sketch, "E11.3.3.3", {"start": v(-374.67, -241.61) * mm, "end": v(-374.67, -291.26) * mm});
            skLineSegment(sketch, "E11.3.3.4", {"start": v(-417.67, -216.79) * mm, "end": v(-374.67, -241.61) * mm});
            skLineSegment(sketch, "E11.3.3.6", {"start": v(-384.67, -247.39) * mm, "end": v(-384.67, -285.5) * mm});
            skLineSegment(sketch, "E11.3.3.7", {"start": v(-417.67, -228.33) * mm, "end": v(-384.67, -247.39) * mm});
            skLineSegment(sketch, "E11.3.3.8", {"start": v(-450.67, -247.39) * mm, "end": v(-417.67, -228.33) * mm});
            skLineSegment(sketch, "E11.3.3.9", {"start": v(-450.67, -285.5) * mm, "end": v(-450.67, -247.39) * mm});
            skLineSegment(sketch, "E11.3.3.10", {"start": v(-417.67, -304.54) * mm, "end": v(-450.67, -285.5) * mm});
            skLineSegment(sketch, "E11.3.3.11", {"start": v(-384.67, -285.5) * mm, "end": v(-417.67, -304.54) * mm});
            skCircle(sketch, "E11.3.3.12", {"center": v(-417.67, -266.44) * mm, "radius": 33 * mm, "construction": true});
            skPoint(sketch, "E11.3.3.13", {"position": v(-401.17, -295.02) * mm});
            skLineSegment(sketch, "E11.3.4.1", {"start": v(-417.98, -365.56) * mm, "end": v(-460.98, -390.39) * mm});
            skLineSegment(sketch, "E11.3.4.3", {"start": v(-417.98, -315.91) * mm, "end": v(-417.98, -365.56) * mm});
            skLineSegment(sketch, "E11.3.4.4", {"start": v(-460.98, -291.09) * mm, "end": v(-417.98, -315.91) * mm});
            skLineSegment(sketch, "E11.3.4.6", {"start": v(-427.98, -321.69) * mm, "end": v(-427.98, -359.8) * mm});
            skLineSegment(sketch, "E11.3.4.7", {"start": v(-460.98, -302.63) * mm, "end": v(-427.98, -321.69) * mm});
            skLineSegment(sketch, "E11.3.4.11", {"start": v(-427.98, -359.8) * mm, "end": v(-460.98, -378.84) * mm});
            skCircle(sketch, "E11.3.4.12", {"center": v(-460.98, -340.74) * mm, "radius": 33 * mm, "construction": true});
            skLineSegment(sketch, "E11.4.0.0", {"start": v(-373.75, -93.2) * mm, "end": v(-416.75, -68.37) * mm});
            skLineSegment(sketch, "E11.4.0.1", {"start": v(-330.75, -68.37) * mm, "end": v(-373.75, -93.2) * mm});
            skLineSegment(sketch, "E11.4.0.2", {"start": v(-416.75, -18.72) * mm, "end": v(-373.75, 6.11) * mm});
            skLineSegment(sketch, "E11.4.0.3", {"start": v(-330.75, -18.72) * mm, "end": v(-330.75, -68.37) * mm});
            skLineSegment(sketch, "E11.4.0.4", {"start": v(-373.75, 6.11) * mm, "end": v(-330.75, -18.72) * mm});
            skLineSegment(sketch, "E11.4.0.5", {"start": v(-416.75, -68.37) * mm, "end": v(-416.75, -18.72) * mm});
            skLineSegment(sketch, "E11.4.0.6", {"start": v(-340.75, -24.49) * mm, "end": v(-340.75, -62.6) * mm});
            skLineSegment(sketch, "E11.4.0.7", {"start": v(-373.75, -5.44) * mm, "end": v(-340.75, -24.49) * mm});
            skLineSegment(sketch, "E11.4.0.8", {"start": v(-406.75, -24.49) * mm, "end": v(-373.75, -5.44) * mm});
            skLineSegment(sketch, "E11.4.0.9", {"start": v(-406.75, -62.6) * mm, "end": v(-406.75, -24.49) * mm});
            skLineSegment(sketch, "E11.4.0.10", {"start": v(-373.75, -81.65) * mm, "end": v(-406.75, -62.6) * mm});
            skLineSegment(sketch, "E11.4.0.11", {"start": v(-340.75, -62.6) * mm, "end": v(-373.75, -81.65) * mm});
            skCircle(sketch, "E11.4.0.12", {"center": v(-373.75, -43.54) * mm, "radius": 33 * mm, "construction": true});
            skPoint(sketch, "E11.4.0.13", {"position": v(-357.25, -72.12) * mm});
            skLineSegment(sketch, "E11.4.1.0", {"start": v(-417.06, -167.5) * mm, "end": v(-460.06, -142.67) * mm});
            skLineSegment(sketch, "E11.4.1.1", {"start": v(-374.06, -142.67) * mm, "end": v(-417.06, -167.5) * mm});
            skLineSegment(sketch, "E11.4.1.2", {"start": v(-460.06, -93.01) * mm, "end": v(-417.06, -68.19) * mm});
            skLineSegment(sketch, "E11.4.1.3", {"start": v(-374.06, -93.01) * mm, "end": v(-374.06, -142.67) * mm});
            skLineSegment(sketch, "E11.4.1.4", {"start": v(-417.06, -68.19) * mm, "end": v(-374.06, -93.01) * mm});
            skLineSegment(sketch, "E11.4.1.6", {"start": v(-384.06, -98.79) * mm, "end": v(-384.06, -136.9) * mm});
            skLineSegment(sketch, "E11.4.1.7", {"start": v(-417.06, -79.74) * mm, "end": v(-384.06, -98.79) * mm});
            skLineSegment(sketch, "E11.4.1.8", {"start": v(-450.06, -98.79) * mm, "end": v(-417.06, -79.74) * mm});
            skLineSegment(sketch, "E11.4.1.9", {"start": v(-450.06, -136.9) * mm, "end": v(-450.06, -98.79) * mm});
            skLineSegment(sketch, "E11.4.1.10", {"start": v(-417.06, -155.95) * mm, "end": v(-450.06, -136.9) * mm});
            skLineSegment(sketch, "E11.4.1.11", {"start": v(-384.06, -136.9) * mm, "end": v(-417.06, -155.95) * mm});
            skCircle(sketch, "E11.4.1.12", {"center": v(-417.06, -117.84) * mm, "radius": 33 * mm, "construction": true});
            skPoint(sketch, "E11.4.1.13", {"position": v(-400.56, -146.42) * mm});
            skLineSegment(sketch, "E11.4.2.1", {"start": v(-417.37, -216.97) * mm, "end": v(-460.37, -241.8) * mm});
            skLineSegment(sketch, "E11.4.2.3", {"start": v(-417.37, -167.31) * mm, "end": v(-417.37, -216.97) * mm});
            skLineSegment(sketch, "E11.4.2.4", {"start": v(-460.37, -142.49) * mm, "end": v(-417.37, -167.31) * mm});
            skLineSegment(sketch, "E11.4.2.6", {"start": v(-427.37, -173.09) * mm, "end": v(-427.37, -211.2) * mm});
            skLineSegment(sketch, "E11.4.2.7", {"start": v(-460.37, -154.03) * mm, "end": v(-427.37, -173.09) * mm});
            skLineSegment(sketch, "E11.4.2.11", {"start": v(-427.37, -211.2) * mm, "end": v(-460.37, -230.24) * mm});
            skCircle(sketch, "E11.4.2.12", {"center": v(-460.37, -192.14) * mm, "radius": 33 * mm, "construction": true});
            skLineSegment(sketch, "E11.direction1", {"start": v(-72.75, -68.37) * mm, "end": v(-158.75, -68.37) * mm, "construction": true});
            skLineSegment(sketch, "E11.direction2", {"start": v(-72.75, -68.37) * mm, "end": v(-116.06, -142.67) * mm, "construction": true});
            skLineSegment(sketch, "E12.0", {"start": v(-5.53, -30) * mm, "end": v(-320, -30) * mm});
            skArc(sketch, "E13.0", {"start": v(-420, -130) * mm, "mid": v(-390.71, -59.29) * mm, "end": v(-320, -30) * mm});
            skLineSegment(sketch, "E14.0", {"start": v(-420, -130) * mm, "end": v(-420, -347.62) * mm});
            skArc(sketch, "E15.0", {"start": v(-409.4, -351.48) * mm, "mid": v(-416.05, -353.26) * mm, "end": v(-420, -347.62) * mm});
            skFitSpline(sketch, "E16.0", {"points": [v(-450, -400) * mm, v(-297.58, -218.34) * mm, v(3.15, 140.09) * mm, v(275.62, -221.62) * mm, v(410, -400) * mm]});
            skSolve(sketch);
        }
        {
            var Q0;
            {var subQ9=sQuery(id+"F4.wireOp",EDGE,"E11.3.1.2");Q0=makeQuery(id+"F4.imprint","IMPRINT",FACE,{"disambiguationData":[TD([[makeQuery(id+"F4.imprint","IMPRINT",EDGE,{"derivedFrom":subQ9}),1.0]])]});}
            var Q1;
            {var subQ11=sQuery(id+"F4.wireOp",EDGE,"E11.2.1.2");Q1=makeQuery(id+"F4.imprint","IMPRINT",FACE,{"disambiguationData":[TD([[makeQuery(id+"F4.imprint","IMPRINT",EDGE,{"derivedFrom":subQ11}),1.0]])]});}
            var Q2;
            {var subQ6=sQuery(id+"F4.wireOp",EDGE,"E11.1.1.2");Q2=makeQuery(id+"F4.imprint","IMPRINT",FACE,{"disambiguationData":[TD([[makeQuery(id+"F4.imprint","IMPRINT",EDGE,{"derivedFrom":subQ6}),1.0]])]});}
            var Q3;
            {var subQ0=sQuery(id+"F4.wireOp",EDGE,"E11.1.0.10");Q3=makeQuery(id+"F4.imprint","IMPRINT",FACE,{"disambiguationData":[TD([[makeQuery(id+"F4.imprint","IMPRINT",EDGE,{"derivedFrom":subQ0}),1.0]])]});}
            var Q4;
            {var subQ1=sQuery(id+"F4.wireOp",EDGE,"E11.1.1.8");Q4=makeQuery(id+"F4.imprint","IMPRINT",FACE,{"disambiguationData":[TD([[makeQuery(id+"F4.imprint","IMPRINT",EDGE,{"derivedFrom":subQ1}),1.0]])]});}
            var Q5;
            Q5=makeQuery(id+"F4.imprint","IMPRINT",FACE,{"disambiguationData":[TD([[makeQuery(id+"F4.imprint","IMPRINT",EDGE,{"derivedFrom":sQuery(id+"F4.wireOp",EDGE,"E11.2.1.6")}),1.0]])]});
            var Q6;
            {var subQ1=sQuery(id+"F4.wireOp",EDGE,"E11.2.2.2");Q6=makeQuery(id+"F4.imprint","IMPRINT",FACE,{"disambiguationData":[TD([[makeQuery(id+"F4.imprint","IMPRINT",EDGE,{"derivedFrom":subQ1}),1.0]])]});}
            var Q7;
            {var subQ5=sQuery(id+"F4.wireOp",EDGE,"E11.3.2.4");var subQ7=sQuery(id+"F4.wireOp",EDGE,"E11.3.2.2");var subQ8=makeQuery(id+"F4.imprint","INTERSECT",VERTEX,{"derivedFrom":[subQ7,subQ5]});Q7=makeQuery(id+"F4.imprint","IMPRINT",FACE,{"disambiguationData":[TD([[makeQuery(id+"F4.imprint","IMPRINT",EDGE,{"disambiguationData":[TD([[subQ8,1.0]])],"derivedFrom":subQ7}),1.0]])]});}
            var Q8;
            {var subQ1=sQuery(id+"F4.wireOp",EDGE,"E11.2.3.2");Q8=makeQuery(id+"F4.imprint","IMPRINT",FACE,{"disambiguationData":[TD([[makeQuery(id+"F4.imprint","IMPRINT",EDGE,{"derivedFrom":subQ1}),1.0]])]});}
            var Q9;
            {var subQ15=sQuery(id+"F4.wireOp",EDGE,"E11.2.2.7");Q9=makeQuery(id+"F4.imprint","IMPRINT",FACE,{"disambiguationData":[TD([[makeQuery(id+"F4.imprint","IMPRINT",EDGE,{"derivedFrom":subQ15}),1.0]])]});}
            var Q10;
            {var subQ5=sQuery(id+"F4.wireOp",EDGE,"E11.2.3.8");Q10=makeQuery(id+"F4.imprint","IMPRINT",FACE,{"disambiguationData":[TD([[makeQuery(id+"F4.imprint","IMPRINT",EDGE,{"derivedFrom":subQ5}),1.0]])]});}
            var Q11;
            {var subQ12=sQuery(id+"F4.wireOp",EDGE,"E11.3.3.6");Q11=makeQuery(id+"F4.imprint","IMPRINT",FACE,{"disambiguationData":[TD([[makeQuery(id+"F4.imprint","IMPRINT",EDGE,{"derivedFrom":subQ12}),1.0]])]});}
            var Q12;
            {var subQ5=sQuery(id+"F4.wireOp",EDGE,"E11.2.4.8");var subQ6=sQuery(id+"F4.wireOp",EDGE,"E11.2.4.7");var subQ7=makeQuery(id+"F4.imprint","INTERSECT",VERTEX,{"derivedFrom":[subQ6,subQ5]});Q12=makeQuery(id+"F4.imprint","IMPRINT",FACE,{"disambiguationData":[TD([[makeQuery(id+"F4.imprint","IMPRINT",EDGE,{"disambiguationData":[TD([[subQ7,-1.0]])],"derivedFrom":subQ6}),1.0]])]});}
            var Q13;
            {var subQ0=sQuery(id+"F4.wireOp",EDGE,"E11.3.4.6");Q13=makeQuery(id+"F4.imprint","IMPRINT",FACE,{"disambiguationData":[TD([[makeQuery(id+"F4.imprint","IMPRINT",EDGE,{"derivedFrom":subQ0}),1.0]])]});}
            var Q14;
            {var subQ10=sQuery(id+"F4.wireOp",EDGE,"E11.4.2.6");Q14=makeQuery(id+"F4.imprint","IMPRINT",FACE,{"disambiguationData":[TD([[makeQuery(id+"F4.imprint","IMPRINT",EDGE,{"derivedFrom":subQ10}),1.0]])]});}
            var Q15;
            {var subQ0=sQuery(id+"F4.wireOp",EDGE,"E16.0");var subQ1=sQuery(id+"F4.wireOp",EDGE,"E9.2");var subQ2=makeQuery(id+"F4.imprint","INTERSECT",VERTEX,{"derivedFrom":[subQ1,subQ0]});Q15=makeQuery(id+"F4.imprint","IMPRINT",FACE,{"disambiguationData":[TD([[makeQuery(id+"F4.imprint","IMPRINT",EDGE,{"disambiguationData":[TD([[subQ2,-1.0]])],"derivedFrom":subQ1}),1.0]])]});}
            var Q16;
            {var subQ5=sQuery(id+"F4.wireOp",EDGE,"E11.2.2.2");Q16=makeQuery(id+"F4.imprint","IMPRINT",FACE,{"disambiguationData":[TD([[makeQuery(id+"F4.imprint","IMPRINT",EDGE,{"derivedFrom":subQ5}),-1.0]])]});}
            var Q17;
            {var subQ5=sQuery(id+"F4.wireOp",EDGE,"E11.2.3.2");Q17=makeQuery(id+"F4.imprint","IMPRINT",FACE,{"disambiguationData":[TD([[makeQuery(id+"F4.imprint","IMPRINT",EDGE,{"derivedFrom":subQ5}),-1.0]])]});}
            var Q18;
            {var subQ4=sQuery(id+"F4.wireOp",EDGE,"E11.3.1.2");Q18=makeQuery(id+"F4.imprint","IMPRINT",FACE,{"disambiguationData":[TD([[makeQuery(id+"F4.imprint","IMPRINT",EDGE,{"derivedFrom":subQ4}),-1.0]])]});}
            var Q19;
            {var subQ1=sQuery(id+"F4.wireOp",EDGE,"E11.2.1.2");Q19=makeQuery(id+"F4.imprint","IMPRINT",FACE,{"disambiguationData":[TD([[makeQuery(id+"F4.imprint","IMPRINT",EDGE,{"derivedFrom":subQ1}),-1.0]])]});}
            var Q20;
            {var subQ2=sQuery(id+"F4.wireOp",EDGE,"E11.1.1.2");Q20=makeQuery(id+"F4.imprint","IMPRINT",FACE,{"disambiguationData":[TD([[makeQuery(id+"F4.imprint","IMPRINT",EDGE,{"derivedFrom":subQ2}),-1.0]])]});}
            var Q21;
            {var subQ0=sQuery(id+"F4.wireOp",EDGE,"E11.2.1.1");var subQ1=sQuery(id+"F4.wireOp",EDGE,"E11.2.1.0");var subQ2=makeQuery(id+"F4.imprint","INTERSECT",VERTEX,{"derivedFrom":[subQ1,subQ0]});Q21=makeQuery(id+"F4.imprint","IMPRINT",FACE,{"disambiguationData":[TD([[makeQuery(id+"F4.imprint","IMPRINT",EDGE,{"disambiguationData":[TD([[subQ2,-1.0]])],"derivedFrom":subQ1}),-1.0]])]});}
            var Q22;
            {var subQ3=sQuery(id+"F4.wireOp",EDGE,"E11.3.2.4");var subQ7=sQuery(id+"F4.wireOp",EDGE,"E11.3.2.2");var subQ8=makeQuery(id+"F4.imprint","INTERSECT",VERTEX,{"derivedFrom":[subQ7,subQ3]});Q22=makeQuery(id+"F4.imprint","IMPRINT",FACE,{"disambiguationData":[TD([[makeQuery(id+"F4.imprint","IMPRINT",EDGE,{"disambiguationData":[TD([[subQ8,1.0]])],"derivedFrom":subQ7}),-1.0]])]});}
            var Q23;
            {var subQ3=sQuery(id+"F4.wireOp",EDGE,"E11.2.4.4");var subQ5=sQuery(id+"F4.wireOp",EDGE,"E11.2.4.2");var subQ6=makeQuery(id+"F4.imprint","INTERSECT",VERTEX,{"derivedFrom":[subQ5,subQ3]});Q23=makeQuery(id+"F4.imprint","IMPRINT",FACE,{"disambiguationData":[TD([[makeQuery(id+"F4.imprint","IMPRINT",EDGE,{"disambiguationData":[TD([[subQ6,1.0]])],"derivedFrom":subQ5}),-1.0]])]});}
            var Q24;
            {var subQ0=sQuery(id+"F4.wireOp",EDGE,"E12.0");var subQ1=sQuery(id+"F4.wireOp",EDGE,"E11.1.0.3");var subQ2=makeQuery(id+"F4.imprint","INTERSECT",VERTEX,{"derivedFrom":[subQ1,subQ0]});Q24=makeQuery(id+"F4.imprint","IMPRINT",FACE,{"disambiguationData":[TD([[makeQuery(id+"F4.imprint","IMPRINT",EDGE,{"disambiguationData":[TD([[subQ2,-1.0]])],"derivedFrom":subQ1}),-1.0]])]});}
            var Q25;
            {var subQ5=sQuery(id+"F4.wireOp",EDGE,"E11.3.3.4");var subQ6=sQuery(id+"F4.wireOp",EDGE,"E11.3.3.2");var subQ7=makeQuery(id+"F4.imprint","INTERSECT",VERTEX,{"derivedFrom":[subQ6,subQ5]});Q25=makeQuery(id+"F4.imprint","IMPRINT",FACE,{"disambiguationData":[TD([[makeQuery(id+"F4.imprint","IMPRINT",EDGE,{"disambiguationData":[TD([[subQ7,1.0]])],"derivedFrom":subQ6}),1.0]])]});}
            var Q26;
            {var subQ0=sQuery(id+"F4.wireOp",EDGE,"E14.0");var subQ1=sQuery(id+"F4.wireOp",EDGE,"E11.3.3.0");var subQ2=makeQuery(id+"F4.imprint","INTERSECT",VERTEX,{"derivedFrom":[subQ1,subQ0]});Q26=makeQuery(id+"F4.imprint","IMPRINT",FACE,{"disambiguationData":[TD([[makeQuery(id+"F4.imprint","IMPRINT",EDGE,{"disambiguationData":[TD([[subQ2,1.0]])],"derivedFrom":subQ1}),1.0]])]});}
            var Q27;
            {var subQ1=sQuery(id+"F4.wireOp",EDGE,"E11.2.1.7");Q27=makeQuery(id+"F4.imprint","IMPRINT",FACE,{"disambiguationData":[TD([[makeQuery(id+"F4.imprint","IMPRINT",EDGE,{"derivedFrom":subQ1}),1.0]])]});}
            var Q28;
            {var subQ5=sQuery(id+"F4.wireOp",EDGE,"E11.3.3.4");var subQ6=sQuery(id+"F4.wireOp",EDGE,"E11.3.3.2");var subQ7=makeQuery(id+"F4.imprint","INTERSECT",VERTEX,{"derivedFrom":[subQ6,subQ5]});Q28=makeQuery(id+"F4.imprint","IMPRINT",FACE,{"disambiguationData":[TD([[makeQuery(id+"F4.imprint","IMPRINT",EDGE,{"disambiguationData":[TD([[subQ7,1.0]])],"derivedFrom":subQ6}),-1.0]])]});}
            var Q29;
            {var subQ0=sQuery(id+"F4.wireOp",EDGE,"E14.0");var subQ1=sQuery(id+"F4.wireOp",EDGE,"E11.4.1.0");var subQ2=makeQuery(id+"F4.imprint","INTERSECT",VERTEX,{"derivedFrom":[subQ1,subQ0]});Q29=makeQuery(id+"F4.imprint","IMPRINT",FACE,{"disambiguationData":[TD([[makeQuery(id+"F4.imprint","IMPRINT",EDGE,{"disambiguationData":[TD([[subQ2,1.0]])],"derivedFrom":subQ1}),-1.0]])]});}
            var Q30;
            {var subQ0=sQuery(id+"F4.wireOp",EDGE,"E14.0");var subQ1=sQuery(id+"F4.wireOp",EDGE,"E11.3.3.0");var subQ2=makeQuery(id+"F4.imprint","INTERSECT",VERTEX,{"derivedFrom":[subQ1,subQ0]});Q30=makeQuery(id+"F4.imprint","IMPRINT",FACE,{"disambiguationData":[TD([[makeQuery(id+"F4.imprint","IMPRINT",EDGE,{"disambiguationData":[TD([[subQ2,1.0]])],"derivedFrom":subQ1}),-1.0]])]});}
            var Q31;
            {var subQ1=sQuery(id+"F4.wireOp",EDGE,"E11.2.0.0");var subQ3=sQuery(id+"F4.wireOp",EDGE,"E11.2.1.3");var subQ4=makeQuery(id+"F4.imprint","INTERSECT",VERTEX,{"derivedFrom":[subQ1,subQ3]});Q31=makeQuery(id+"F4.imprint","IMPRINT",FACE,{"disambiguationData":[TD([[makeQuery(id+"F4.imprint","IMPRINT",EDGE,{"disambiguationData":[TD([[subQ4,-1.0]])],"derivedFrom":subQ1}),-1.0]])]});}
            var Q32;
            {var subQ1=sQuery(id+"F4.wireOp",EDGE,"E11.3.0.0");var subQ3=sQuery(id+"F4.wireOp",EDGE,"E11.3.1.3");var subQ4=makeQuery(id+"F4.imprint","INTERSECT",VERTEX,{"derivedFrom":[subQ1,subQ3]});Q32=makeQuery(id+"F4.imprint","IMPRINT",FACE,{"disambiguationData":[TD([[makeQuery(id+"F4.imprint","IMPRINT",EDGE,{"disambiguationData":[TD([[subQ4,-1.0]])],"derivedFrom":subQ1}),-1.0]])]});}
            var Q33;
            {var subQ0=sQuery(id+"F4.wireOp",EDGE,"E13.0");var subQ1=sQuery(id+"F4.wireOp",EDGE,"E11.4.0.0");var subQ2=makeQuery(id+"F4.imprint","INTERSECT",VERTEX,{"derivedFrom":[subQ1,subQ0]});Q33=makeQuery(id+"F4.imprint","IMPRINT",FACE,{"disambiguationData":[TD([[makeQuery(id+"F4.imprint","IMPRINT",EDGE,{"disambiguationData":[TD([[subQ2,1.0]])],"derivedFrom":subQ1}),-1.0]])]});}
            var Q34;
            {var subQ1=sQuery(id+"F4.wireOp",EDGE,"E11.3.1.0");var subQ3=sQuery(id+"F4.wireOp",EDGE,"E11.3.2.3");var subQ4=makeQuery(id+"F4.imprint","INTERSECT",VERTEX,{"derivedFrom":[subQ1,subQ3]});Q34=makeQuery(id+"F4.imprint","IMPRINT",FACE,{"disambiguationData":[TD([[makeQuery(id+"F4.imprint","IMPRINT",EDGE,{"disambiguationData":[TD([[subQ4,-1.0]])],"derivedFrom":subQ1}),-1.0]])]});}
            var Q35;
            {var subQ1=sQuery(id+"F4.wireOp",EDGE,"E11.2.1.0");var subQ3=sQuery(id+"F4.wireOp",EDGE,"E11.2.2.3");var subQ4=makeQuery(id+"F4.imprint","INTERSECT",VERTEX,{"derivedFrom":[subQ1,subQ3]});Q35=makeQuery(id+"F4.imprint","IMPRINT",FACE,{"disambiguationData":[TD([[makeQuery(id+"F4.imprint","IMPRINT",EDGE,{"disambiguationData":[TD([[subQ4,-1.0]])],"derivedFrom":subQ1}),-1.0]])]});}
            var Q36;
            {var subQ0=sQuery(id+"F4.wireOp",EDGE,"E11.3.2.3");var subQ5=sQuery(id+"F4.wireOp",EDGE,"E11.2.3.4");var subQ6=makeQuery(id+"F4.imprint","INTERSECT",VERTEX,{"derivedFrom":[subQ5,subQ0]});Q36=makeQuery(id+"F4.imprint","IMPRINT",FACE,{"disambiguationData":[TD([[makeQuery(id+"F4.imprint","IMPRINT",EDGE,{"disambiguationData":[TD([[subQ6,-1.0]])],"derivedFrom":subQ5}),-1.0]])]});}
            var Q37;
            {var subQ1=sQuery(id+"F4.wireOp",EDGE,"E11.3.2.0");var subQ3=sQuery(id+"F4.wireOp",EDGE,"E11.3.3.3");var subQ4=makeQuery(id+"F4.imprint","INTERSECT",VERTEX,{"derivedFrom":[subQ1,subQ3]});Q37=makeQuery(id+"F4.imprint","IMPRINT",FACE,{"disambiguationData":[TD([[makeQuery(id+"F4.imprint","IMPRINT",EDGE,{"disambiguationData":[TD([[subQ4,-1.0]])],"derivedFrom":subQ1}),-1.0]])]});}
            var Q38;
            {var subQ0=sQuery(id+"F4.wireOp",EDGE,"E11.3.3.3");var subQ5=sQuery(id+"F4.wireOp",EDGE,"E11.2.4.4");var subQ6=makeQuery(id+"F4.imprint","INTERSECT",VERTEX,{"derivedFrom":[subQ5,subQ0]});Q38=makeQuery(id+"F4.imprint","IMPRINT",FACE,{"disambiguationData":[TD([[makeQuery(id+"F4.imprint","IMPRINT",EDGE,{"disambiguationData":[TD([[subQ6,-1.0]])],"derivedFrom":subQ5}),-1.0]])]});}
            var Q39;
            {var subQ0=sQuery(id+"F4.wireOp",EDGE,"E11.2.0.3");var subQ5=sQuery(id+"F4.wireOp",EDGE,"E11.1.1.4");var subQ6=makeQuery(id+"F4.imprint","INTERSECT",VERTEX,{"derivedFrom":[subQ5,subQ0]});Q39=makeQuery(id+"F4.imprint","IMPRINT",FACE,{"disambiguationData":[TD([[makeQuery(id+"F4.imprint","IMPRINT",EDGE,{"disambiguationData":[TD([[subQ6,-1.0]])],"derivedFrom":subQ5}),-1.0]])]});}
            extrude(context, id + "F5", {"entities" : qUnion([Q0, Q1, Q2, Q3, Q4, Q5, Q6, Q7, Q8, Q9, Q10, Q11, Q12, Q13, Q14, Q15, Q16, Q17, Q18, Q19, Q20, Q21, Q22, Q23, Q24, Q25, Q26, Q27, Q28, Q29, Q30, Q31, Q32, Q33, Q34, Q35, Q36, Q37, Q38, Q39]), "operationType" : NewBodyOperationType.ADD, "depth" : 400 * mm, "offsetDistance" : 25 * mm});
        }
    });
